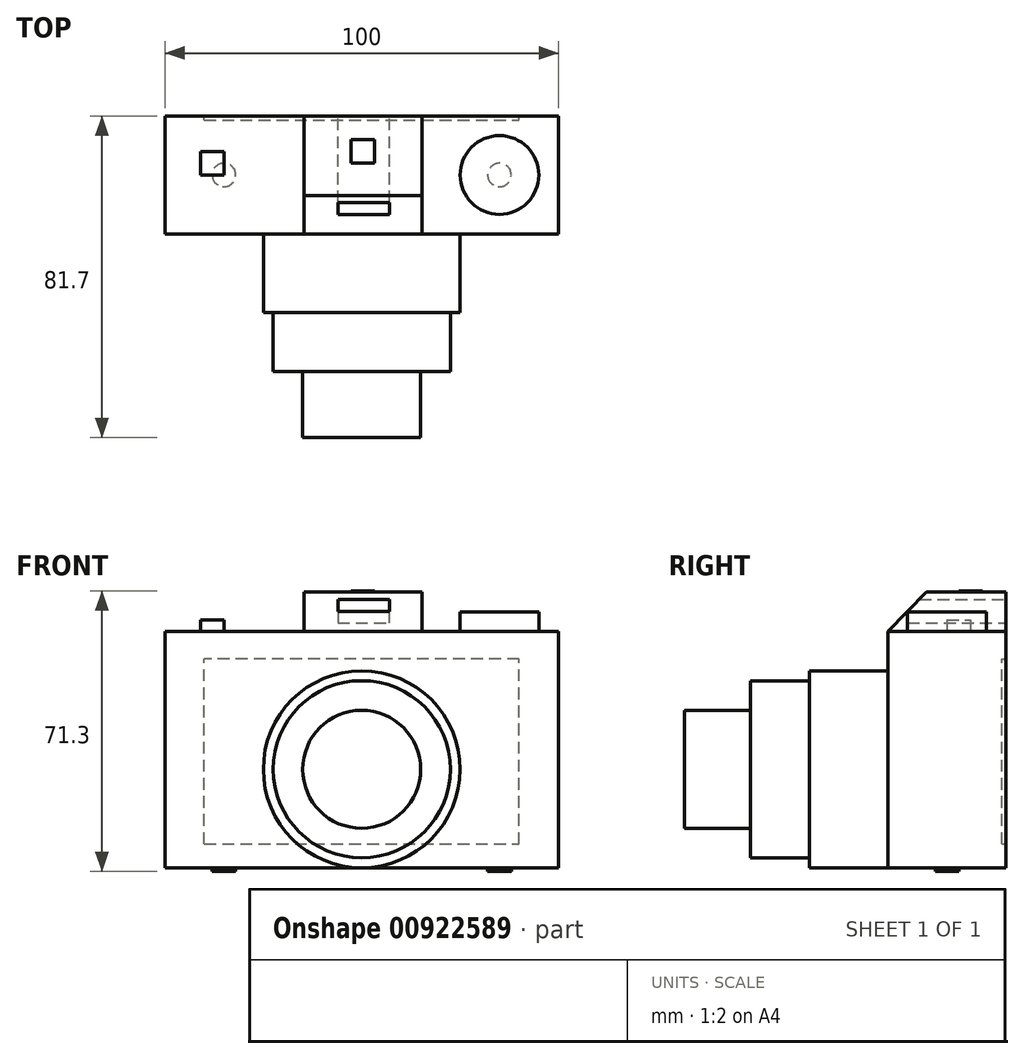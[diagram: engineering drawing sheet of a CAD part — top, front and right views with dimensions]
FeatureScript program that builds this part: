
annotation { "Feature Type Name" : "Feature", "Feature Type Description" : "" }
export const myFeature = defineFeature(function(context is Context, id is Id, definition is map)
    precondition{}
    {
        {
            var Q0;
            Q0=qCreatedBy(makeId("Top.planeOp"),FACE);
            var sketch = newSketch(context, id + "F0", { "sketchPlane" : qUnion([Q0])});
            skLineSegment(sketch, "E0", {"start": v(-70.65, 1.99) * mm, "end": v(29.35, 1.99) * mm});
            skLineSegment(sketch, "E1", {"start": v(29.35, 1.99) * mm, "end": v(29.35, -28.01) * mm});
            skLineSegment(sketch, "E2", {"start": v(29.35, -28.01) * mm, "end": v(-70.65, -28.01) * mm});
            skLineSegment(sketch, "E3", {"start": v(-70.65, -28.01) * mm, "end": v(-70.65, 1.99) * mm});
            skSolve(sketch);
        }
        {
            var Q0;
            Q0 = qSketchRegion(id + "F0", true);
            extrude(context, id + "F1", {"entities" : qUnion([Q0]), "oppositeDirection" : true, "depth" : 60 * mm, "offsetDistance" : 25 * mm});
        }
        {
            var Q0;
            Q0=makeQuery(id+"F1.opExtrude","CAP_FACE",FACE,{"disambiguationData":[OSD([sQuery(id+"F0.wireOp",EDGE,"E0"),sQuery(id+"F0.wireOp",EDGE,"E1"),sQuery(id+"F0.wireOp",EDGE,"E2"),sQuery(id+"F0.wireOp",EDGE,"E3")])],"isStart":true});
            var sketch = newSketch(context, id + "F2", { "sketchPlane" : qUnion([Q0])});
            skLineSegment(sketch, "E4", {"start": v(-61.65, -7.01) * mm, "end": v(-55.65, -7.01) * mm});
            skLineSegment(sketch, "E5", {"start": v(-55.65, -7.01) * mm, "end": v(-55.65, -13.01) * mm});
            skLineSegment(sketch, "E6", {"start": v(-55.65, -13.01) * mm, "end": v(-61.65, -13.01) * mm});
            skLineSegment(sketch, "E7", {"start": v(-61.65, -13.01) * mm, "end": v(-61.65, -7.01) * mm});
            skSolve(sketch);
        }
        {
            var Q0;
            Q0 = qSketchRegion(id + "F2", true);
            extrude(context, id + "F3", {"entities" : qUnion([Q0]), "operationType" : NewBodyOperationType.ADD, "depth" : 2.9 * mm, "offsetDistance" : 25 * mm});
        }
        {
            var Q0;
            Q0=makeQuery(id+"F1.opExtrude","CAP_FACE",FACE,{"disambiguationData":[OSD([sQuery(id+"F0.wireOp",EDGE,"E0"),sQuery(id+"F0.wireOp",EDGE,"E1"),sQuery(id+"F0.wireOp",EDGE,"E2"),sQuery(id+"F0.wireOp",EDGE,"E3")])],"isStart":true});
            var sketch = newSketch(context, id + "F4", { "sketchPlane" : qUnion([Q0])});
            skLineSegment(sketch, "E8", {"start": v(-35.3, 1.99) * mm, "end": v(-35.3, -28.01) * mm});
            skLineSegment(sketch, "E9", {"start": v(-35.3, -28.01) * mm, "end": v(-5.3, -28.01) * mm});
            skLineSegment(sketch, "E10", {"start": v(-5.3, -28.01) * mm, "end": v(-5.3, 1.99) * mm});
            skLineSegment(sketch, "E11", {"start": v(-5.3, 1.99) * mm, "end": v(-35.3, 1.99) * mm});
            skSolve(sketch);
        }
        {
            var Q0;
            Q0 = qSketchRegion(id + "F4", true);
            extrude(context, id + "F5", {"entities" : qUnion([Q0]), "operationType" : NewBodyOperationType.ADD, "depth" : 10 * mm, "offsetDistance" : 25 * mm});
        }
        {
            var Q0;
            Q0=makeQuery(id+"F5.opExtrude","SWEPT_FACE",FACE,{"disambiguationData":[OSD([sQuery(id+"F4.wireOp",EDGE,"E10")])]});
            var sketch = newSketch(context, id + "F6", { "sketchPlane" : qUnion([Q0])});
            skLineSegment(sketch, "E12", {"start": v(-28.01, 10) * mm, "end": v(-18.24, 10) * mm});
            skLineSegment(sketch, "E13", {"start": v(-18.24, 10) * mm, "end": v(-28.01, 0) * mm});
            skLineSegment(sketch, "E14", {"start": v(-28.01, 0) * mm, "end": v(-28.01, 10) * mm});
            skSolve(sketch);
        }
        {
            var Q0;
            Q0 = qSketchRegion(id + "F6", true);
            extrude(context, id + "F7", {"entities" : qUnion([Q0]), "operationType" : NewBodyOperationType.REMOVE, "oppositeDirection" : true, "depth" : 30 * mm, "offsetDistance" : 25 * mm});
        }
        {
            var Q0;
            {var subQ0=sQuery(id+"F0.wireOp",EDGE,"E2");var subQ1=sQuery(id+"F0.wireOp",EDGE,"E1");var subQ2=sQuery(id+"F0.wireOp",EDGE,"E0");Q0=makeQuery(id+"F5.boolean.opBoolean","SPLIT",FACE,{"disambiguationData":[TD([makeQuery(id+"F1.opExtrude","SWEPT_FACE",FACE,{"disambiguationData":[OSD([subQ1])]})])],"derivedFrom":makeQuery(id+"F1.opExtrude","CAP_FACE",FACE,{"disambiguationData":[OSD([subQ2,subQ1,subQ0,sQuery(id+"F0.wireOp",EDGE,"E3")])],"isStart":true})});}
            var sketch = newSketch(context, id + "F8", { "sketchPlane" : qUnion([Q0])});
            skCircle(sketch, "E15", {"center": v(14.35, -13.01) * mm, "radius": 10 * mm});
            skSolve(sketch);
        }
        {
            var Q0;
            Q0 = qSketchRegion(id + "F8", true);
            extrude(context, id + "F9", {"entities" : qUnion([Q0]), "operationType" : NewBodyOperationType.ADD, "depth" : 5 * mm, "offsetDistance" : 25 * mm});
        }
        {
            var Q0;
            Q0=makeQuery(id+"F5.boolean.opBoolean","MERGE",FACE,{"derivedFrom":[makeQuery(id+"F1.opExtrude","SWEPT_FACE",FACE,{"disambiguationData":[OSD([sQuery(id+"F0.wireOp",EDGE,"E2")])]}),makeQuery(id+"F5.opExtrude","SWEPT_FACE",FACE,{"disambiguationData":[OSD([sQuery(id+"F4.wireOp",EDGE,"E9")])]})]});
            var sketch = newSketch(context, id + "F10", { "sketchPlane" : qUnion([Q0])});
            skCircle(sketch, "E16", {"center": v(-20.65, -35) * mm, "radius": 25 * mm});
            skSolve(sketch);
        }
        {
            var Q0;
            Q0 = qSketchRegion(id + "F10", true);
            extrude(context, id + "F11", {"entities" : qUnion([Q0]), "operationType" : NewBodyOperationType.ADD, "depth" : 20 * mm, "offsetDistance" : 25 * mm});
        }
        {
            var Q0;
            Q0=makeQuery(id+"F5.boolean.opBoolean","MERGE",FACE,{"derivedFrom":[makeQuery(id+"F1.opExtrude","SWEPT_FACE",FACE,{"disambiguationData":[OSD([sQuery(id+"F0.wireOp",EDGE,"E0")])]}),makeQuery(id+"F5.opExtrude","SWEPT_FACE",FACE,{"disambiguationData":[OSD([sQuery(id+"F4.wireOp",EDGE,"E11")])]})]});
            var sketch = newSketch(context, id + "F12", { "sketchPlane" : qUnion([Q0])});
            skLineSegment(sketch, "E17", {"start": v(13.55, 8.16) * mm, "end": v(26.7, 8.16) * mm});
            skLineSegment(sketch, "E18", {"start": v(26.7, 8.16) * mm, "end": v(26.7, 2.22) * mm});
            skLineSegment(sketch, "E19", {"start": v(26.7, 2.22) * mm, "end": v(13.55, 2.22) * mm});
            skLineSegment(sketch, "E20", {"start": v(13.55, 2.22) * mm, "end": v(13.55, 8.16) * mm});
            skSolve(sketch);
        }
        {
            var Q0;
            Q0 = qSketchRegion(id + "F12", true);
            extrude(context, id + "F13", {"entities" : qUnion([Q0]), "operationType" : NewBodyOperationType.REMOVE, "oppositeDirection" : true, "depth" : 25 * mm, "offsetDistance" : 25 * mm});
        }
        {
            var Q0;
            Q0=makeQuery(id+"F5.boolean.opBoolean","MERGE",FACE,{"derivedFrom":[makeQuery(id+"F1.opExtrude","SWEPT_FACE",FACE,{"disambiguationData":[OSD([sQuery(id+"F0.wireOp",EDGE,"E0")])]}),makeQuery(id+"F5.opExtrude","SWEPT_FACE",FACE,{"disambiguationData":[OSD([sQuery(id+"F4.wireOp",EDGE,"E11")])]})]});
            var sketch = newSketch(context, id + "F14", { "sketchPlane" : qUnion([Q0])});
            skLineSegment(sketch, "E21", {"start": v(-19.35, -6.96) * mm, "end": v(60.65, -6.96) * mm});
            skLineSegment(sketch, "E22", {"start": v(60.65, -54) * mm, "end": v(-19.35, -54) * mm});
            skLineSegment(sketch, "E23", {"start": v(-19.35, -54) * mm, "end": v(-19.35, -6.96) * mm});
            skLineSegment(sketch, "E24", {"start": v(60.65, -54) * mm, "end": v(60.65, -6.96) * mm});
            skSolve(sketch);
        }
        {
            var Q0;
            Q0 = qSketchRegion(id + "F14", true);
            extrude(context, id + "F15", {"entities" : qUnion([Q0]), "operationType" : NewBodyOperationType.REMOVE, "oppositeDirection" : true, "depth" : 1 * mm, "offsetDistance" : 25 * mm});
        }
        {
            var Q0;
            Q0=makeQuery(id+"F1.opExtrude","CAP_FACE",FACE,{"disambiguationData":[OSD([sQuery(id+"F0.wireOp",EDGE,"E0"),sQuery(id+"F0.wireOp",EDGE,"E1"),sQuery(id+"F0.wireOp",EDGE,"E2"),sQuery(id+"F0.wireOp",EDGE,"E3")])],"isStart":false});
            var sketch = newSketch(context, id + "F16", { "sketchPlane" : qUnion([Q0])});
            skCircle(sketch, "E25", {"center": v(-55.65, 13.01) * mm, "radius": 3 * mm});
            skCircle(sketch, "E26", {"center": v(14.35, 13.01) * mm, "radius": 3 * mm});
            skSolve(sketch);
        }
        {
            var Q0;
            Q0 = qSketchRegion(id + "F16", true);
            extrude(context, id + "F17", {"entities" : qUnion([Q0]), "operationType" : NewBodyOperationType.ADD, "depth" : 1 * mm, "offsetDistance" : 25 * mm});
        }
        {
            var Q0;
            Q0=makeQuery(id+"F5.opExtrude","CAP_FACE",FACE,{"disambiguationData":[OSD([sQuery(id+"F4.wireOp",EDGE,"E8"),sQuery(id+"F4.wireOp",EDGE,"E9"),sQuery(id+"F4.wireOp",EDGE,"E10"),sQuery(id+"F4.wireOp",EDGE,"E11")])],"isStart":false});
            var sketch = newSketch(context, id + "F18", { "sketchPlane" : qUnion([Q0])});
            skLineSegment(sketch, "E27", {"start": v(-23.4, -3.98) * mm, "end": v(-17.4, -3.98) * mm});
            skLineSegment(sketch, "E28", {"start": v(-17.4, -3.98) * mm, "end": v(-17.4, -9.98) * mm});
            skLineSegment(sketch, "E29", {"start": v(-17.4, -9.98) * mm, "end": v(-23.4, -9.98) * mm});
            skLineSegment(sketch, "E30", {"start": v(-23.4, -9.98) * mm, "end": v(-23.4, -3.98) * mm});
            skSolve(sketch);
        }
        {
            var Q0;
            Q0 = qSketchRegion(id + "F18", true);
            extrude(context, id + "F19", {"entities" : qUnion([Q0]), "operationType" : NewBodyOperationType.ADD, "depth" : 0.3 * mm, "offsetDistance" : 25 * mm});
        }
        {
            var Q0;
            Q0=makeQuery(id+"F11.opExtrude","CAP_FACE",FACE,{"disambiguationData":[OSD([sQuery(id+"F10.wireOp",EDGE,"E16")])],"isStart":false});
            var sketch = newSketch(context, id + "F20", { "sketchPlane" : qUnion([Q0])});
            skCircle(sketch, "E31", {"center": v(-20.65, -35) * mm, "radius": 22.5 * mm});
            skSolve(sketch);
        }
        {
            var Q0;
            Q0 = qSketchRegion(id + "F20", true);
            extrude(context, id + "F21", {"entities" : qUnion([Q0]), "operationType" : NewBodyOperationType.ADD, "depth" : 15 * mm, "offsetDistance" : 25 * mm});
        }
        {
            var Q0;
            Q0=makeQuery(id+"F21.opExtrude","CAP_FACE",FACE,{"disambiguationData":[OSD([sQuery(id+"F20.wireOp",EDGE,"E31")])],"isStart":false});
            var sketch = newSketch(context, id + "F22", { "sketchPlane" : qUnion([Q0])});
            skCircle(sketch, "E32", {"center": v(-20.65, -35) * mm, "radius": 15 * mm});
            skSolve(sketch);
        }
        {
            var Q0;
            Q0 = qSketchRegion(id + "F22", true);
            extrude(context, id + "F23", {"entities" : qUnion([Q0]), "operationType" : NewBodyOperationType.ADD, "depth" : 16.7 * mm, "offsetDistance" : 25 * mm});
        }
    });
